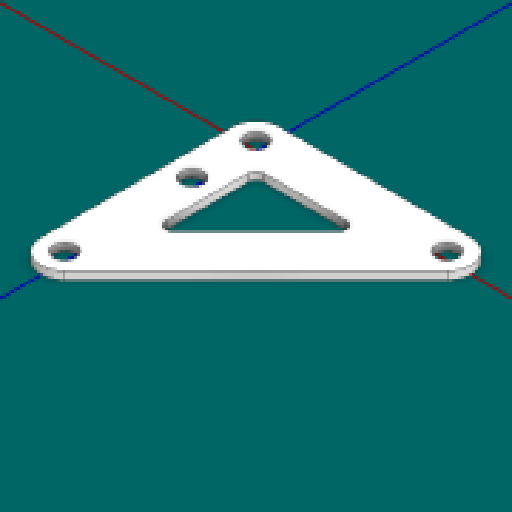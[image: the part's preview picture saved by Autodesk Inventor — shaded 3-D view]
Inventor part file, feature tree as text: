
AUTODESK INVENTOR PART (.ipt)
format: ipt  version: 2025 (Build 290162000, 162)  size: 122,368 bytes
history: native  units: in
note: dims shown in document units (in); Inventor stores cm internally (conversion verified against a paired STEP export)
features: other x3, extrude x1, sketch x1
ambient origin geometry x8: Origin, YZ Plane, XZ Plane, XY Plane, X Axis, Y Axis, Z Axis, Center Point
bodies: Solid1 (feature_tree)
feature tree (5):
  other  "Blocks"
  extrude  "Extrusion1"  Depth=0.375in
  sketch  "Sketch1"  dims[d0=0.375in d1=0.375in d2=0.375in d3=0.0625in d4=0.0in d5=0.375in d6=0.0625in d7=0.0625in d11=0.172in]
  other  "main"
  other  "main:1"
